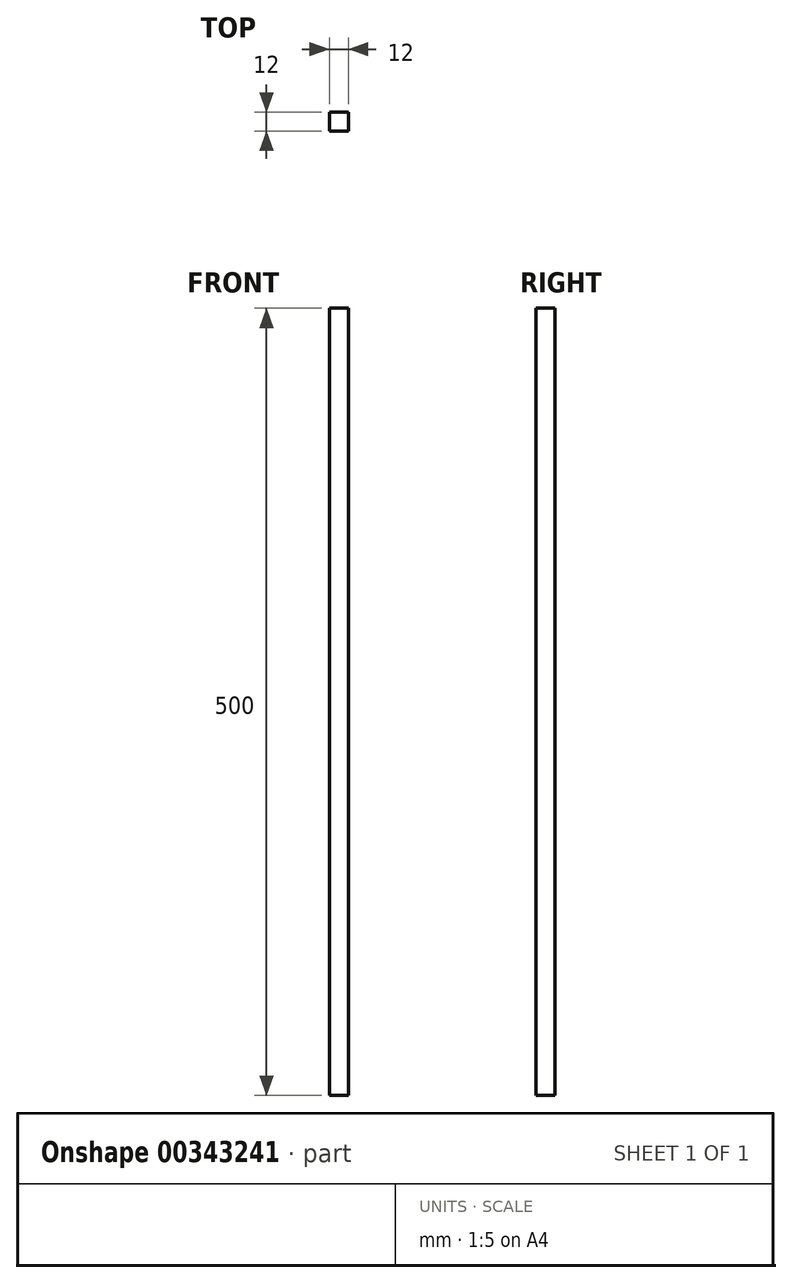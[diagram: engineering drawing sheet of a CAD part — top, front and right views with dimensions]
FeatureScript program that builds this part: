
annotation { "Feature Type Name" : "Feature", "Feature Type Description" : "" }
export const myFeature = defineFeature(function(context is Context, id is Id, definition is map)
    precondition{}
    {
        {
            var Q0;
            Q0=qCreatedBy(makeId("Top.planeOp"),FACE);
            var sketch = newSketch(context, id + "F0", { "sketchPlane" : qUnion([Q0])});
            skLineSegment(sketch, "E0.bottom", {"start": v(6, 6) * mm, "end": v(-6, 6) * mm});
            skLineSegment(sketch, "E0.top", {"start": v(6, -6) * mm, "end": v(-6, -6) * mm});
            skLineSegment(sketch, "E0.left", {"start": v(6, 6) * mm, "end": v(6, -6) * mm});
            skLineSegment(sketch, "E0.right", {"start": v(-6, 6) * mm, "end": v(-6, -6) * mm});
            skPoint(sketch, "E0.middle", {"position": v(0, 0) * mm});
            skSolve(sketch);
        }
        {
            var Q0;
            Q0=makeQuery(id+"F0.imprint","IMPRINT",FACE,{"disambiguationData":[TD([[makeQuery(id+"F0.imprint","IMPRINT",EDGE,{"derivedFrom":sQuery(id+"F0.wireOp",EDGE,"E0.bottom")}),1.0]])]});
            extrude(context, id + "F1", {"entities" : qUnion([Q0]), "endBound" : BoundingType.SYMMETRIC, "depth" : 500 * mm});
        }
    });
